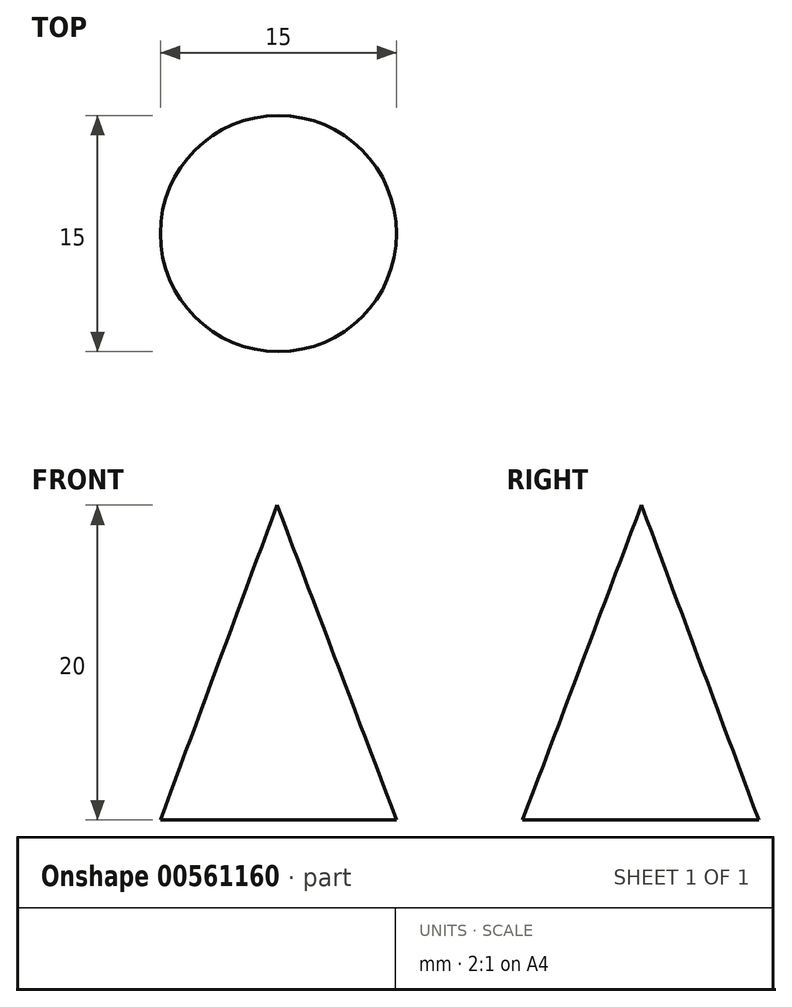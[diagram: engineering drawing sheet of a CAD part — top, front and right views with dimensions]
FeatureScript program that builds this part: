
annotation { "Feature Type Name" : "Feature", "Feature Type Description" : "" }
export const myFeature = defineFeature(function(context is Context, id is Id, definition is map)
    precondition{}
    {
        {
            var Q0;
            Q0=qCreatedBy(makeId("Top.planeOp"),FACE);
            var sketch = newSketch(context, id + "F0", { "sketchPlane" : qUnion([Q0])});
            skCircle(sketch, "E0", {"center": v(-29.88, 11.11) * mm, "radius": 7.5 * mm});
            skSolve(sketch);
        }
        {
            var Q0;
            Q0=qCreatedBy(makeId("Top.planeOp"),FACE);
            cPlane(context, id + "F1", {"entities" : qUnion([Q0]), "cplaneType" : CPlaneType.OFFSET, "offset" : 20 * mm, "width" : 150 * mm, "height" : 150 * mm});
        }
        {
            var Q0;
            Q0=qCreatedBy(id+"F1.planeOp",FACE);
            var sketch = newSketch(context, id + "F2", { "sketchPlane" : qUnion([Q0])});
            skPoint(sketch, "E1", {"position": v(-29.97, 11.16) * mm});
            skSolve(sketch);
        }
        {
            var Q0;
            Q0=sQuery(id+"F2.wireOp",VERTEX,"E1");
            var Q1;
            Q1=makeQuery(id+"F0.imprint","IMPRINT",FACE,{"disambiguationData":[TD([[makeQuery(id+"F0.imprint","IMPRINT",EDGE,{"derivedFrom":sQuery(id+"F0.wireOp",EDGE,"E0")}),1.0]])]});
            loft(context, id + "F3", {"sheetProfilesArray" : [{ "sheetProfileEntities" : qUnion([Q0]) }, { "sheetProfileEntities" : qUnion([Q1]) }]});
        }
    });
